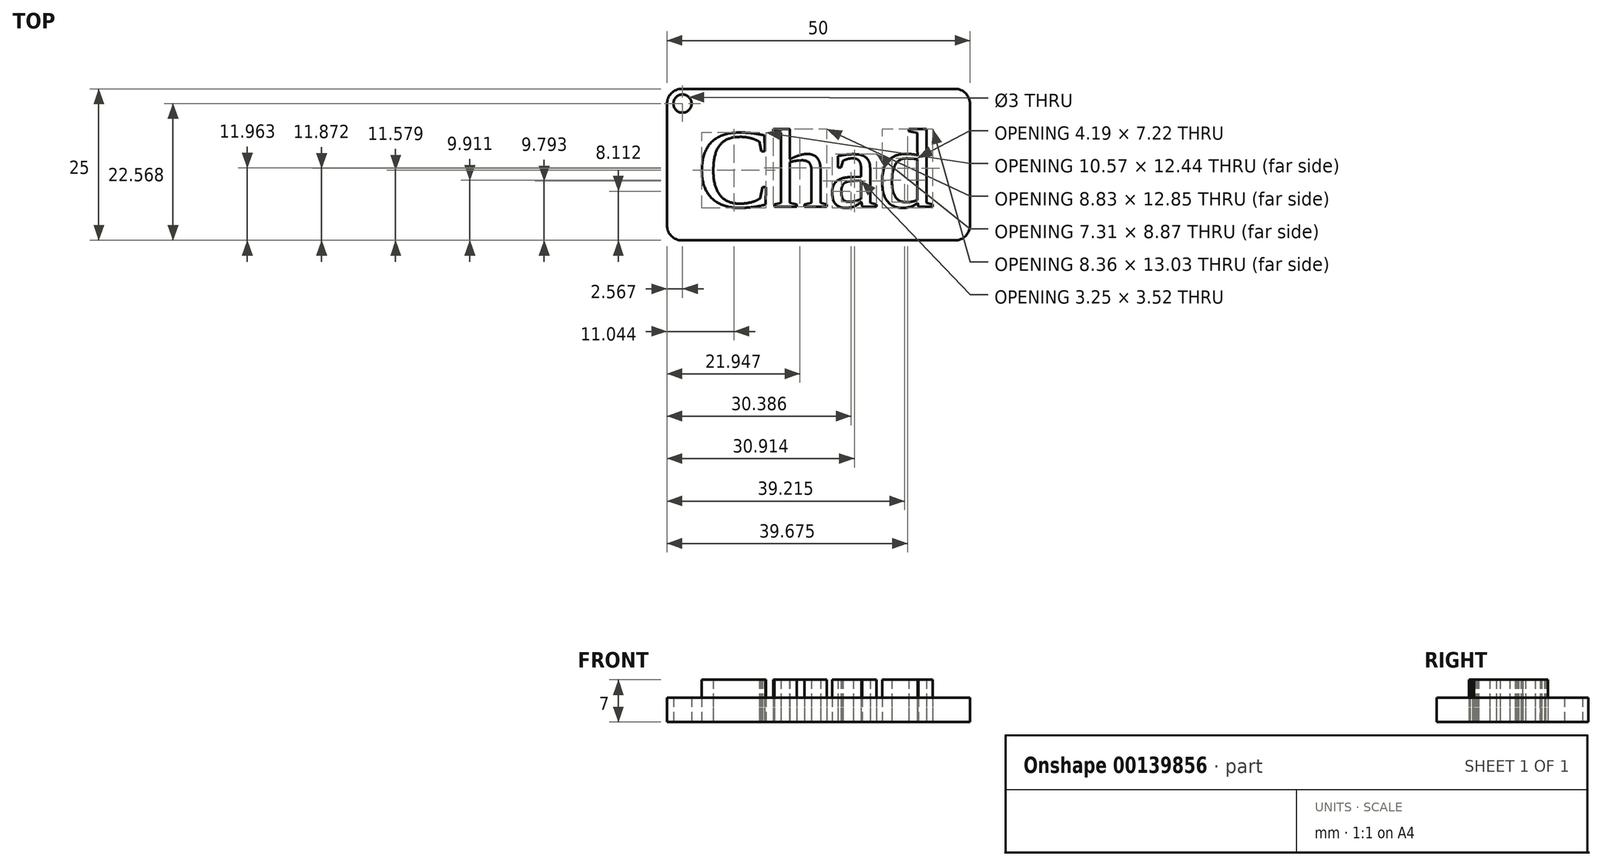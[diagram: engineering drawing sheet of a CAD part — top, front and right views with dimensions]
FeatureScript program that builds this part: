
annotation { "Feature Type Name" : "Feature", "Feature Type Description" : "" }
export const myFeature = defineFeature(function(context is Context, id is Id, definition is map)
    precondition{}
    {
        {
            var Q0;
            Q0=qCreatedBy(makeId("Top.planeOp"),FACE);
            var sketch = newSketch(context, id + "F0", { "sketchPlane" : qUnion([Q0])});
            skLineSegment(sketch, "E0.bottom", {"start": v(25, -12.5) * mm, "end": v(-25, -12.5) * mm});
            skLineSegment(sketch, "E0.top", {"start": v(25, 12.5) * mm, "end": v(-25, 12.5) * mm});
            skLineSegment(sketch, "E0.left", {"start": v(25, -12.5) * mm, "end": v(25, 12.5) * mm});
            skLineSegment(sketch, "E0.right", {"start": v(-25, -12.5) * mm, "end": v(-25, 12.5) * mm});
            skPoint(sketch, "E0.middle", {"position": v(0, 0) * mm});
            skText(sketch, "E1", { "text": "Chad", "fontName": "Tinos-Regular.ttf"});
            skCircle(sketch, "E2", {"center": v(-22.43, 10.07) * mm, "radius": 1.5 * mm});
            const initialGuessF0  = {"E1": [-0.02, -0.00696, 1, 0, 0.01333]};
            skSetInitialGuess(sketch, initialGuessF0);
            skSolve(sketch);
        }
        {
            var Q0;
            Q0 = qSketchRegion(id + "F0", true);
            var Q1;
            Q1=makeQuery(id+"F0.imprint","IMPRINT",FACE,{"disambiguationData":[TD([[makeQuery(id+"F0.imprint","IMPRINT",EDGE,{"derivedFrom":sQuery(id+"F0.wireOp",EDGE,"E1.sketch_text.stroke-66")}),1.0]])]});
            var Q2;
            Q2=makeQuery(id+"F0.imprint","IMPRINT",FACE,{"disambiguationData":[TD([[makeQuery(id+"F0.imprint","IMPRINT",EDGE,{"derivedFrom":sQuery(id+"F0.wireOp",EDGE,"E1.sketch_text.stroke-88")}),1.0]])]});
            extrude(context, id + "F1", {"entities" : qUnion([Q0, Q1, Q2]), "depth" : 4 * mm});
        }
        {
            var Q0;
            Q0=makeQuery(id+"F0.imprint","IMPRINT",FACE,{"disambiguationData":[TD([[makeQuery(id+"F0.imprint","IMPRINT",EDGE,{"derivedFrom":sQuery(id+"F0.wireOp",EDGE,"E1.sketch_text.stroke-73")}),-1.0]])]});
            var Q1;
            Q1=makeQuery(id+"F0.imprint","IMPRINT",FACE,{"disambiguationData":[TD([[makeQuery(id+"F0.imprint","IMPRINT",EDGE,{"derivedFrom":sQuery(id+"F0.wireOp",EDGE,"E1.sketch_text.stroke-45")}),-1.0]])]});
            var Q2;
            Q2=makeQuery(id+"F0.imprint","IMPRINT",FACE,{"disambiguationData":[TD([[makeQuery(id+"F0.imprint","IMPRINT",EDGE,{"derivedFrom":sQuery(id+"F0.wireOp",EDGE,"E1.sketch_text.stroke-20")}),-1.0]])]});
            var Q3;
            Q3=makeQuery(id+"F0.imprint","IMPRINT",FACE,{"disambiguationData":[TD([[makeQuery(id+"F0.imprint","IMPRINT",EDGE,{"derivedFrom":sQuery(id+"F0.wireOp",EDGE,"E1.sketch_text.stroke-0")}),-1.0]])]});
            extrude(context, id + "F2", {"entities" : qUnion([Q0, Q1, Q2, Q3]), "depth" : 7 * mm});
        }
        {
            var Q0;
            Q0=makeQuery(id+"F1.opExtrude","SWEPT_EDGE",EDGE,{"disambiguationData":[OSD([sQuery(id+"F0.wireOp",EDGE,"E0.top"),sQuery(id+"F0.wireOp",EDGE,"E0.left")])]});
            var Q1;
            Q1=makeQuery(id+"F1.opExtrude","SWEPT_EDGE",EDGE,{"disambiguationData":[OSD([sQuery(id+"F0.wireOp",EDGE,"E0.bottom"),sQuery(id+"F0.wireOp",EDGE,"E0.left")])]});
            var Q2;
            Q2=makeQuery(id+"F1.opExtrude","SWEPT_EDGE",EDGE,{"disambiguationData":[OSD([sQuery(id+"F0.wireOp",EDGE,"E0.top"),sQuery(id+"F0.wireOp",EDGE,"E0.right")])]});
            var Q3;
            Q3=makeQuery(id+"F1.opExtrude","SWEPT_EDGE",EDGE,{"disambiguationData":[OSD([sQuery(id+"F0.wireOp",EDGE,"E0.bottom"),sQuery(id+"F0.wireOp",EDGE,"E0.right")])]});
            fillet(context, id + "F3", {"entities" : qUnion([Q0, Q1, Q2, Q3]), "radius" : 2.5 * mm, "tangentPropagation" : true, "allowEdgeOverflow" : false});
        }
    });
